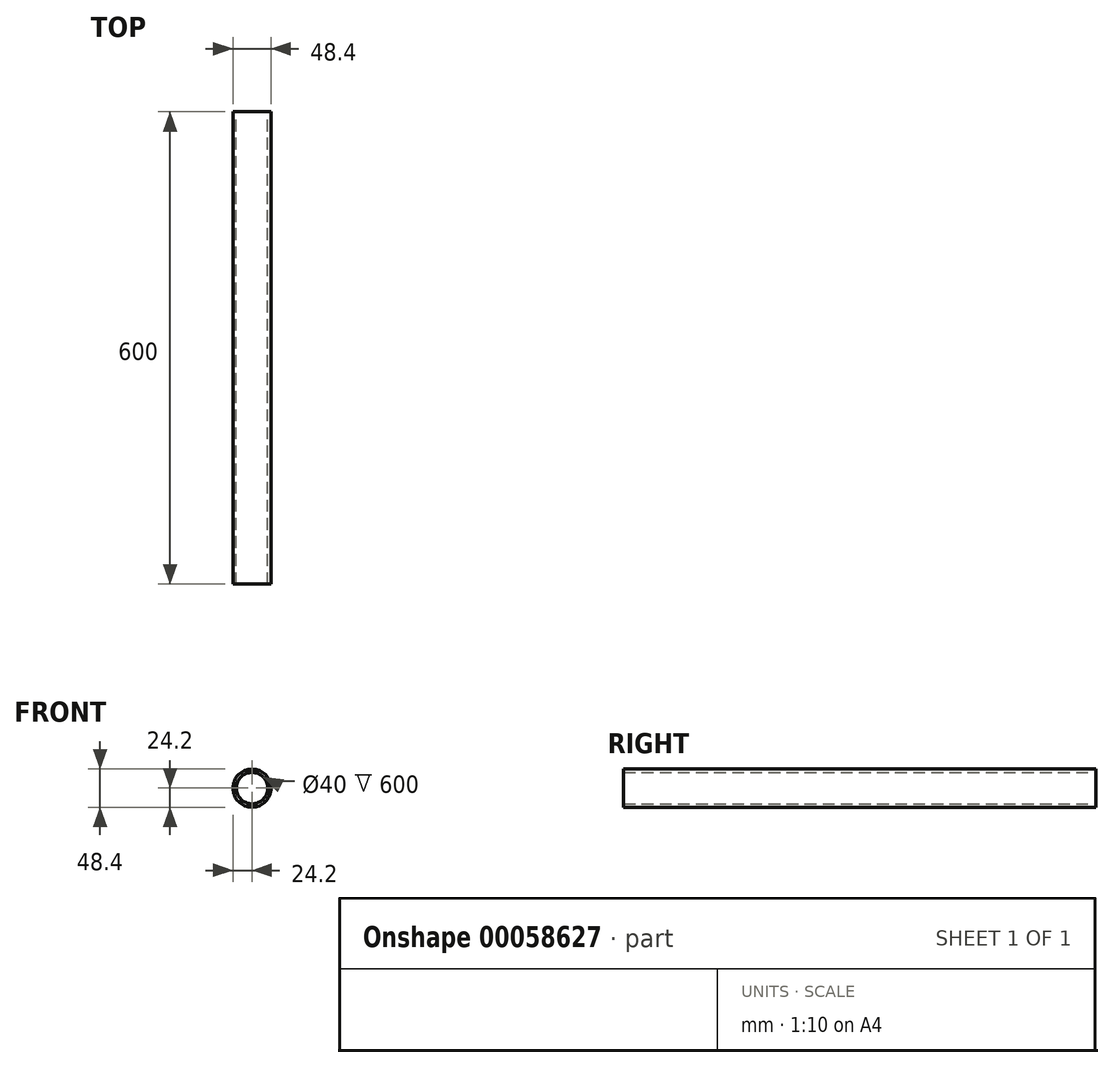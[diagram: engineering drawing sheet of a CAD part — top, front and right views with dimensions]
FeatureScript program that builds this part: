
annotation { "Feature Type Name" : "Feature", "Feature Type Description" : "" }
export const myFeature = defineFeature(function(context is Context, id is Id, definition is map)
    precondition{}
    {
        {
            var Q0;
            Q0=qCreatedBy(makeId("Front.planeOp"),FACE);
            var sketch = newSketch(context, id + "F0", { "sketchPlane" : qUnion([Q0])});
            skCircle(sketch, "E0", {"center": v(0, 0) * mm, "radius": 24.2 * mm});
            skCircle(sketch, "E1", {"center": v(0, 0) * mm, "radius": 20 * mm});
            skSolve(sketch);
        }
        {
            var Q0;
            Q0=makeQuery(id+"F0.imprint","IMPRINT",FACE,{"disambiguationData":[TD([[makeQuery(id+"F0.imprint","IMPRINT",EDGE,{"derivedFrom":sQuery(id+"F0.wireOp",EDGE,"E0")}),1.0]])]});
            extrude(context, id + "F1", {"entities" : qUnion([Q0]), "depth" : 600 * mm});
        }
    });
